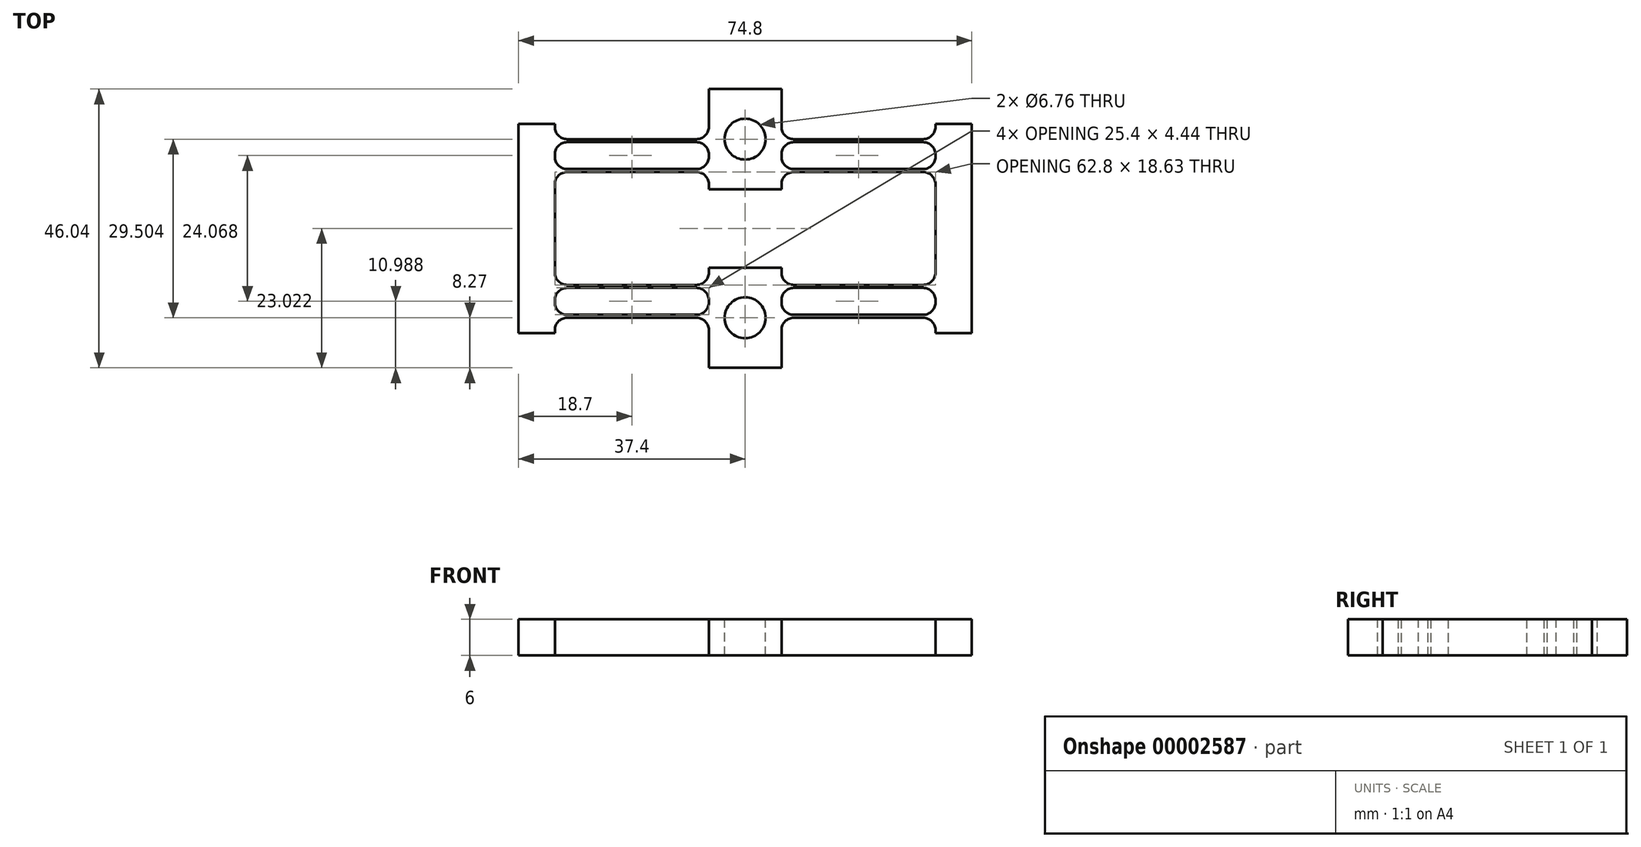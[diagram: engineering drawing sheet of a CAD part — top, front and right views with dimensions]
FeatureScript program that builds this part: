
annotation { "Feature Type Name" : "Feature", "Feature Type Description" : "" }
export const myFeature = defineFeature(function(context is Context, id is Id, definition is map)
    precondition{}
    {
        {
            var Q0;
            Q0=qCreatedBy(makeId("Top.planeOp"),FACE);
            var sketch = newSketch(context, id + "F0", { "sketchPlane" : qUnion([Q0])});
            skLineSegment(sketch, "E0.bottom", {"start": v(6, -8.27) * mm, "end": v(-6, -8.27) * mm});
            skLineSegment(sketch, "E0.top", {"start": v(6, 8.27) * mm, "end": v(-6, 8.27) * mm});
            skLineSegment(sketch, "E0.left", {"start": v(6, -8.27) * mm, "end": v(6, 8.27) * mm});
            skLineSegment(sketch, "E0.right", {"start": v(-6, -8.27) * mm, "end": v(-6, 8.27) * mm});
            skPoint(sketch, "E0.middle", {"position": v(0, 0) * mm});
            skLineSegment(sketch, "E1.bottom", {"start": v(6, 0.5) * mm, "end": v(31.4, 0.5) * mm});
            skLineSegment(sketch, "E1.top", {"start": v(6, 0) * mm, "end": v(31.4, 0) * mm});
            skLineSegment(sketch, "E1.left", {"start": v(6, 0.5) * mm, "end": v(6, 0) * mm});
            skLineSegment(sketch, "E1.right", {"start": v(31.4, 0.5) * mm, "end": v(31.4, 0) * mm});
            skLineSegment(sketch, "E2.bottom", {"start": v(31.4, -2.52) * mm, "end": v(37.4, -2.52) * mm});
            skLineSegment(sketch, "E2.top", {"start": v(31.4, 32.02) * mm, "end": v(37.4, 32.02) * mm});
            skLineSegment(sketch, "E2.left", {"start": v(31.4, -2.52) * mm, "end": v(31.4, 32.02) * mm});
            skLineSegment(sketch, "E2.right", {"start": v(37.4, -2.52) * mm, "end": v(37.4, 32.02) * mm});
            skLineSegment(sketch, "E3.bottom", {"start": v(6, 5.44) * mm, "end": v(31.4, 5.44) * mm});
            skLineSegment(sketch, "E3.top", {"start": v(6, 4.94) * mm, "end": v(31.4, 4.94) * mm});
            skLineSegment(sketch, "E3.left", {"start": v(6, 5.44) * mm, "end": v(6, 4.94) * mm});
            skLineSegment(sketch, "E3.right", {"start": v(31.4, 5.44) * mm, "end": v(31.4, 4.94) * mm});
            skLineSegment(sketch, "E4", {"start": v(0, 0) * mm, "end": v(0, 28.75) * mm, "construction": true});
            skLineSegment(sketch, "E5", {"start": v(31.4, 14.75) * mm, "end": v(-20.14, 14.75) * mm, "construction": true});
            skPoint(sketch, "E5.endSnap0", {"position": v(31.4, 14.75) * mm});
            skLineSegment(sketch, "E6.MirrorCS", {"start": v(-31.4, 0.5) * mm, "end": v(-31.4, 0) * mm});
            skLineSegment(sketch, "E7.MirrorCS", {"start": v(-31.4, 5.44) * mm, "end": v(-31.4, 4.94) * mm});
            skLineSegment(sketch, "E8.MirrorCS", {"start": v(-31.4, 32.02) * mm, "end": v(-37.4, 32.02) * mm});
            skLineSegment(sketch, "E9.MirrorCS", {"start": v(-31.4, -2.52) * mm, "end": v(-37.4, -2.52) * mm});
            skLineSegment(sketch, "E10.MirrorCS", {"start": v(-6, 0.5) * mm, "end": v(-31.4, 0.5) * mm});
            skPoint(sketch, "E11.MirrorP", {"position": v(-31.4, 14.75) * mm});
            skLineSegment(sketch, "E12.MirrorCS", {"start": v(-31.4, 14.75) * mm, "end": v(20.14, 14.75) * mm, "construction": true});
            skLineSegment(sketch, "E13.MirrorCS", {"start": v(-6, 4.94) * mm, "end": v(-31.4, 4.94) * mm});
            skLineSegment(sketch, "E14.MirrorCS", {"start": v(-6, 5.44) * mm, "end": v(-31.4, 5.44) * mm});
            skLineSegment(sketch, "E15.MirrorCS", {"start": v(-37.4, -2.52) * mm, "end": v(-37.4, 32.02) * mm});
            skLineSegment(sketch, "E16.MirrorCS", {"start": v(-31.4, -2.52) * mm, "end": v(-31.4, 32.02) * mm});
            skLineSegment(sketch, "E17.MirrorCS", {"start": v(-6, 0) * mm, "end": v(-31.4, 0) * mm});
            skLineSegment(sketch, "E18.MirrorCS", {"start": v(-6, 29) * mm, "end": v(-31.4, 29) * mm});
            skLineSegment(sketch, "E19.MirrorCS", {"start": v(-6, 24.07) * mm, "end": v(-31.4, 24.07) * mm});
            skLineSegment(sketch, "E20.MirrorCS", {"start": v(-6, 24.57) * mm, "end": v(-31.4, 24.57) * mm});
            skLineSegment(sketch, "E21.MirrorCS", {"start": v(-6, 29.5) * mm, "end": v(-31.4, 29.5) * mm});
            skLineSegment(sketch, "E22.MirrorCS", {"start": v(6, 24.57) * mm, "end": v(31.4, 24.57) * mm});
            skLineSegment(sketch, "E23.MirrorCS", {"start": v(6, 29) * mm, "end": v(31.4, 29) * mm});
            skLineSegment(sketch, "E24.MirrorCS", {"start": v(6, 29.5) * mm, "end": v(31.4, 29.5) * mm});
            skLineSegment(sketch, "E25.MirrorCS", {"start": v(6, 24.07) * mm, "end": v(31.4, 24.07) * mm});
            skLineSegment(sketch, "E26.MirrorCS", {"start": v(6, 21.24) * mm, "end": v(-6, 21.24) * mm});
            skLineSegment(sketch, "E27.MirrorCS", {"start": v(-6, 37.77) * mm, "end": v(-6, 21.24) * mm});
            skLineSegment(sketch, "E28.MirrorCS", {"start": v(6, 37.77) * mm, "end": v(-6, 37.77) * mm});
            skLineSegment(sketch, "E29.MirrorCS", {"start": v(6, 37.77) * mm, "end": v(6, 21.24) * mm});
            skPoint(sketch, "E30.MirrorP", {"position": v(0, 29.5) * mm});
            skSolve(sketch);
        }
        {
            var Q0;
            Q0 = qSketchRegion(id + "F0", true);
            var Q1;
            {var subQ0=sQuery(id+"F0.wireOp",EDGE,"E13.MirrorCS");Q1=makeQuery(id+"F0.imprint","IMPRINT",FACE,{"disambiguationData":[TD([[makeQuery(id+"F0.imprint","IMPRINT",EDGE,{"derivedFrom":subQ0}),-1.0]])]});}
            var Q2;
            Q2=makeQuery(id+"F0.imprint","IMPRINT",FACE,{"disambiguationData":[TD([[makeQuery(id+"F0.imprint","IMPRINT",EDGE,{"derivedFrom":sQuery(id+"F0.wireOp",EDGE,"E3.bottom")}),-1.0]])]});
            var Q3;
            {var subQ0=sQuery(id+"F0.wireOp",EDGE,"E22.MirrorCS");Q3=makeQuery(id+"F0.imprint","IMPRINT",FACE,{"disambiguationData":[TD([[makeQuery(id+"F0.imprint","IMPRINT",EDGE,{"derivedFrom":subQ0}),-1.0]])]});}
            var Q4;
            {var subQ0=sQuery(id+"F0.wireOp",EDGE,"E19.MirrorCS");Q4=makeQuery(id+"F0.imprint","IMPRINT",FACE,{"disambiguationData":[TD([[makeQuery(id+"F0.imprint","IMPRINT",EDGE,{"derivedFrom":subQ0}),-1.0]])]});}
            extrude(context, id + "F1", {"entities" : qUnion([Q0, Q1, Q2, Q3, Q4]), "depth" : 6 * mm, "offsetDistance" : 25 * mm});
        }
        {
            var Q0;
            Q0=sQuery(id+"F0.wireOp",VERTEX,"E30.MirrorP");
            var Q1;
            Q1=sQuery(id+"F0.wireOp",VERTEX,"E0.middle");
            var Q2;
            Q2=makeQuery(id+"F1.opExtrude","SWEPT_BODY",BODY,{"disambiguationData":[OSD([sQuery(id+"F0.wireOp",EDGE,"E0.bottom"),sQuery(id+"F0.wireOp",EDGE,"E0.top"),sQuery(id+"F0.wireOp",EDGE,"E0.left"),sQuery(id+"F0.wireOp",EDGE,"E0.right"),sQuery(id+"F0.wireOp",EDGE,"E1.bottom"),sQuery(id+"F0.wireOp",EDGE,"E1.top"),sQuery(id+"F0.wireOp",EDGE,"E2.bottom"),sQuery(id+"F0.wireOp",EDGE,"E2.top"),sQuery(id+"F0.wireOp",EDGE,"E2.left"),sQuery(id+"F0.wireOp",EDGE,"E2.right"),sQuery(id+"F0.wireOp",EDGE,"E3.bottom"),sQuery(id+"F0.wireOp",EDGE,"E3.top"),sQuery(id+"F0.wireOp",EDGE,"E8.MirrorCS"),sQuery(id+"F0.wireOp",EDGE,"E9.MirrorCS"),sQuery(id+"F0.wireOp",EDGE,"E10.MirrorCS"),sQuery(id+"F0.wireOp",EDGE,"E13.MirrorCS"),sQuery(id+"F0.wireOp",EDGE,"E14.MirrorCS"),sQuery(id+"F0.wireOp",EDGE,"E15.MirrorCS"),sQuery(id+"F0.wireOp",EDGE,"E16.MirrorCS"),sQuery(id+"F0.wireOp",EDGE,"E17.MirrorCS"),sQuery(id+"F0.wireOp",EDGE,"E18.MirrorCS"),sQuery(id+"F0.wireOp",EDGE,"E19.MirrorCS"),sQuery(id+"F0.wireOp",EDGE,"E20.MirrorCS"),sQuery(id+"F0.wireOp",EDGE,"E21.MirrorCS"),sQuery(id+"F0.wireOp",EDGE,"E22.MirrorCS"),sQuery(id+"F0.wireOp",EDGE,"E23.MirrorCS"),sQuery(id+"F0.wireOp",EDGE,"E24.MirrorCS"),sQuery(id+"F0.wireOp",EDGE,"E25.MirrorCS"),sQuery(id+"F0.wireOp",EDGE,"E26.MirrorCS"),sQuery(id+"F0.wireOp",EDGE,"E27.MirrorCS"),sQuery(id+"F0.wireOp",EDGE,"E28.MirrorCS"),sQuery(id+"F0.wireOp",EDGE,"E29.MirrorCS")])]});
            hole(context, id + "F2", {"style" : HoleStyle.SIMPLE, "endStyle" : HoleEndStyle.THROUGH, "oppositeDirection" : true, "standardTappedOrClearance" : lookupTablePath({ "standard" : "ANSI", "fit" : "Normal (ASME)", "size" : "1/4", "type" : "Clearance" }), "standardBlindInLast" : lookupTablePath({ "fit" : "Free", "standard" : "ANSI", "size" : "1/4", "type" : "Clearance" }), "holeDiameter" : 6.76 * mm, "majorDiameter" : 5 * mm, "isTappedThrough" : true, "tappedDepth" : 12 * mm, "tapClearance" : 3, "locations" : qUnion([Q0, Q1]), "scope" : qUnion([Q2])});
        }
        {
            var Q0;
            Q0=makeQuery(id+"F1.opExtrude","SWEPT_EDGE",EDGE,{"disambiguationData":[OSD([sQuery(id+"F0.wireOp",EDGE,"E16.MirrorCS"),sQuery(id+"F0.wireOp",EDGE,"E18.MirrorCS")])]});
            var Q1;
            Q1=makeQuery(id+"F1.opExtrude","SWEPT_EDGE",EDGE,{"disambiguationData":[OSD([sQuery(id+"F0.wireOp",EDGE,"E16.MirrorCS"),sQuery(id+"F0.wireOp",EDGE,"E20.MirrorCS")])]});
            var Q2;
            Q2=makeQuery(id+"F1.opExtrude","SWEPT_EDGE",EDGE,{"disambiguationData":[OSD([sQuery(id+"F0.wireOp",EDGE,"E16.MirrorCS"),sQuery(id+"F0.wireOp",EDGE,"E19.MirrorCS")])]});
            var Q3;
            Q3=makeQuery(id+"F1.opExtrude","SWEPT_EDGE",EDGE,{"disambiguationData":[OSD([sQuery(id+"F0.wireOp",EDGE,"E18.MirrorCS"),sQuery(id+"F0.wireOp",EDGE,"E27.MirrorCS")])]});
            var Q4;
            Q4=makeQuery(id+"F1.opExtrude","SWEPT_EDGE",EDGE,{"disambiguationData":[OSD([sQuery(id+"F0.wireOp",EDGE,"E20.MirrorCS"),sQuery(id+"F0.wireOp",EDGE,"E27.MirrorCS")])]});
            var Q5;
            Q5=makeQuery(id+"F1.opExtrude","SWEPT_EDGE",EDGE,{"disambiguationData":[OSD([sQuery(id+"F0.wireOp",EDGE,"E21.MirrorCS"),sQuery(id+"F0.wireOp",EDGE,"E27.MirrorCS")])]});
            var Q6;
            Q6=makeQuery(id+"F1.opExtrude","SWEPT_EDGE",EDGE,{"disambiguationData":[OSD([sQuery(id+"F0.wireOp",EDGE,"E16.MirrorCS"),sQuery(id+"F0.wireOp",EDGE,"E21.MirrorCS")])]});
            var Q7;
            Q7=makeQuery(id+"F1.opExtrude","SWEPT_EDGE",EDGE,{"disambiguationData":[OSD([sQuery(id+"F0.wireOp",EDGE,"E14.MirrorCS"),sQuery(id+"F0.wireOp",EDGE,"E16.MirrorCS")])]});
            var Q8;
            Q8=makeQuery(id+"F1.opExtrude","SWEPT_EDGE",EDGE,{"disambiguationData":[OSD([sQuery(id+"F0.wireOp",EDGE,"E10.MirrorCS"),sQuery(id+"F0.wireOp",EDGE,"E16.MirrorCS")])]});
            var Q9;
            Q9=makeQuery(id+"F1.opExtrude","SWEPT_EDGE",EDGE,{"disambiguationData":[OSD([sQuery(id+"F0.wireOp",EDGE,"E22.MirrorCS"),sQuery(id+"F0.wireOp",EDGE,"E29.MirrorCS")])]});
            var Q10;
            Q10=makeQuery(id+"F1.opExtrude","SWEPT_EDGE",EDGE,{"disambiguationData":[OSD([sQuery(id+"F0.wireOp",EDGE,"E24.MirrorCS"),sQuery(id+"F0.wireOp",EDGE,"E29.MirrorCS")])]});
            var Q11;
            Q11=makeQuery(id+"F1.opExtrude","SWEPT_EDGE",EDGE,{"disambiguationData":[OSD([sQuery(id+"F0.wireOp",EDGE,"E13.MirrorCS"),sQuery(id+"F0.wireOp",EDGE,"E16.MirrorCS")])]});
            var Q12;
            Q12=makeQuery(id+"F1.opExtrude","SWEPT_EDGE",EDGE,{"disambiguationData":[OSD([sQuery(id+"F0.wireOp",EDGE,"E16.MirrorCS"),sQuery(id+"F0.wireOp",EDGE,"E17.MirrorCS")])]});
            var Q13;
            Q13=makeQuery(id+"F1.opExtrude","SWEPT_EDGE",EDGE,{"disambiguationData":[OSD([sQuery(id+"F0.wireOp",EDGE,"E0.right"),sQuery(id+"F0.wireOp",EDGE,"E17.MirrorCS")])]});
            var Q14;
            Q14=makeQuery(id+"F1.opExtrude","SWEPT_EDGE",EDGE,{"disambiguationData":[OSD([sQuery(id+"F0.wireOp",EDGE,"E0.right"),sQuery(id+"F0.wireOp",EDGE,"E13.MirrorCS")])]});
            var Q15;
            Q15=makeQuery(id+"F1.opExtrude","SWEPT_EDGE",EDGE,{"disambiguationData":[OSD([sQuery(id+"F0.wireOp",EDGE,"E2.left"),sQuery(id+"F0.wireOp",EDGE,"E3.top"),sQuery(id+"F0.wireOp",EDGE,"E3.right")])]});
            var Q16;
            Q16=makeQuery(id+"F1.opExtrude","SWEPT_EDGE",EDGE,{"disambiguationData":[OSD([sQuery(id+"F0.wireOp",EDGE,"E1.top"),sQuery(id+"F0.wireOp",EDGE,"E2.left")])]});
            var Q17;
            Q17=makeQuery(id+"F1.opExtrude","SWEPT_EDGE",EDGE,{"disambiguationData":[OSD([sQuery(id+"F0.wireOp",EDGE,"E2.left"),sQuery(id+"F0.wireOp",EDGE,"E25.MirrorCS")])]});
            var Q18;
            Q18=makeQuery(id+"F1.opExtrude","SWEPT_EDGE",EDGE,{"disambiguationData":[OSD([sQuery(id+"F0.wireOp",EDGE,"E2.left"),sQuery(id+"F0.wireOp",EDGE,"E23.MirrorCS")])]});
            var Q19;
            Q19=makeQuery(id+"F1.opExtrude","SWEPT_EDGE",EDGE,{"disambiguationData":[OSD([sQuery(id+"F0.wireOp",EDGE,"E19.MirrorCS"),sQuery(id+"F0.wireOp",EDGE,"E27.MirrorCS")])]});
            var Q20;
            Q20=makeQuery(id+"F1.opExtrude","SWEPT_EDGE",EDGE,{"disambiguationData":[OSD([sQuery(id+"F0.wireOp",EDGE,"E2.left"),sQuery(id+"F0.wireOp",EDGE,"E24.MirrorCS")])]});
            var Q21;
            Q21=makeQuery(id+"F1.opExtrude","SWEPT_EDGE",EDGE,{"disambiguationData":[OSD([sQuery(id+"F0.wireOp",EDGE,"E2.left"),sQuery(id+"F0.wireOp",EDGE,"E3.bottom"),sQuery(id+"F0.wireOp",EDGE,"E3.right")])]});
            var Q22;
            Q22=makeQuery(id+"F1.opExtrude","SWEPT_EDGE",EDGE,{"disambiguationData":[OSD([sQuery(id+"F0.wireOp",EDGE,"E0.right"),sQuery(id+"F0.wireOp",EDGE,"E14.MirrorCS")])]});
            var Q23;
            Q23=makeQuery(id+"F1.opExtrude","SWEPT_EDGE",EDGE,{"disambiguationData":[OSD([sQuery(id+"F0.wireOp",EDGE,"E0.left"),sQuery(id+"F0.wireOp",EDGE,"E3.bottom"),sQuery(id+"F0.wireOp",EDGE,"E3.left")])]});
            var Q24;
            Q24=makeQuery(id+"F1.opExtrude","SWEPT_EDGE",EDGE,{"disambiguationData":[OSD([sQuery(id+"F0.wireOp",EDGE,"E0.left"),sQuery(id+"F0.wireOp",EDGE,"E1.bottom"),sQuery(id+"F0.wireOp",EDGE,"E1.left")])]});
            var Q25;
            Q25=makeQuery(id+"F1.opExtrude","SWEPT_EDGE",EDGE,{"disambiguationData":[OSD([sQuery(id+"F0.wireOp",EDGE,"E0.left"),sQuery(id+"F0.wireOp",EDGE,"E1.top"),sQuery(id+"F0.wireOp",EDGE,"E1.left")])]});
            var Q26;
            Q26=makeQuery(id+"F1.opExtrude","SWEPT_EDGE",EDGE,{"disambiguationData":[OSD([sQuery(id+"F0.wireOp",EDGE,"E0.left"),sQuery(id+"F0.wireOp",EDGE,"E3.top"),sQuery(id+"F0.wireOp",EDGE,"E3.left")])]});
            var Q27;
            Q27=makeQuery(id+"F1.opExtrude","SWEPT_EDGE",EDGE,{"disambiguationData":[OSD([sQuery(id+"F0.wireOp",EDGE,"E1.bottom"),sQuery(id+"F0.wireOp",EDGE,"E2.left")])]});
            var Q28;
            Q28=makeQuery(id+"F1.opExtrude","SWEPT_EDGE",EDGE,{"disambiguationData":[OSD([sQuery(id+"F0.wireOp",EDGE,"E0.right"),sQuery(id+"F0.wireOp",EDGE,"E10.MirrorCS")])]});
            var Q29;
            Q29=makeQuery(id+"F1.opExtrude","SWEPT_EDGE",EDGE,{"disambiguationData":[OSD([sQuery(id+"F0.wireOp",EDGE,"E2.left"),sQuery(id+"F0.wireOp",EDGE,"E22.MirrorCS")])]});
            var Q30;
            Q30=makeQuery(id+"F1.opExtrude","SWEPT_EDGE",EDGE,{"disambiguationData":[OSD([sQuery(id+"F0.wireOp",EDGE,"E25.MirrorCS"),sQuery(id+"F0.wireOp",EDGE,"E29.MirrorCS")])]});
            var Q31;
            Q31=makeQuery(id+"F1.opExtrude","SWEPT_EDGE",EDGE,{"disambiguationData":[OSD([sQuery(id+"F0.wireOp",EDGE,"E23.MirrorCS"),sQuery(id+"F0.wireOp",EDGE,"E29.MirrorCS")])]});
            fillet(context, id + "F3", {"entities" : qUnion([Q0, Q1, Q2, Q3, Q4, Q5, Q6, Q7, Q8, Q9, Q10, Q11, Q12, Q13, Q14, Q15, Q16, Q17, Q18, Q19, Q20, Q21, Q22, Q23, Q24, Q25, Q26, Q27, Q28, Q29, Q30, Q31]), "radius" : 2 * mm, "tangentPropagation" : true, "allowEdgeOverflow" : false});
        }
    });
